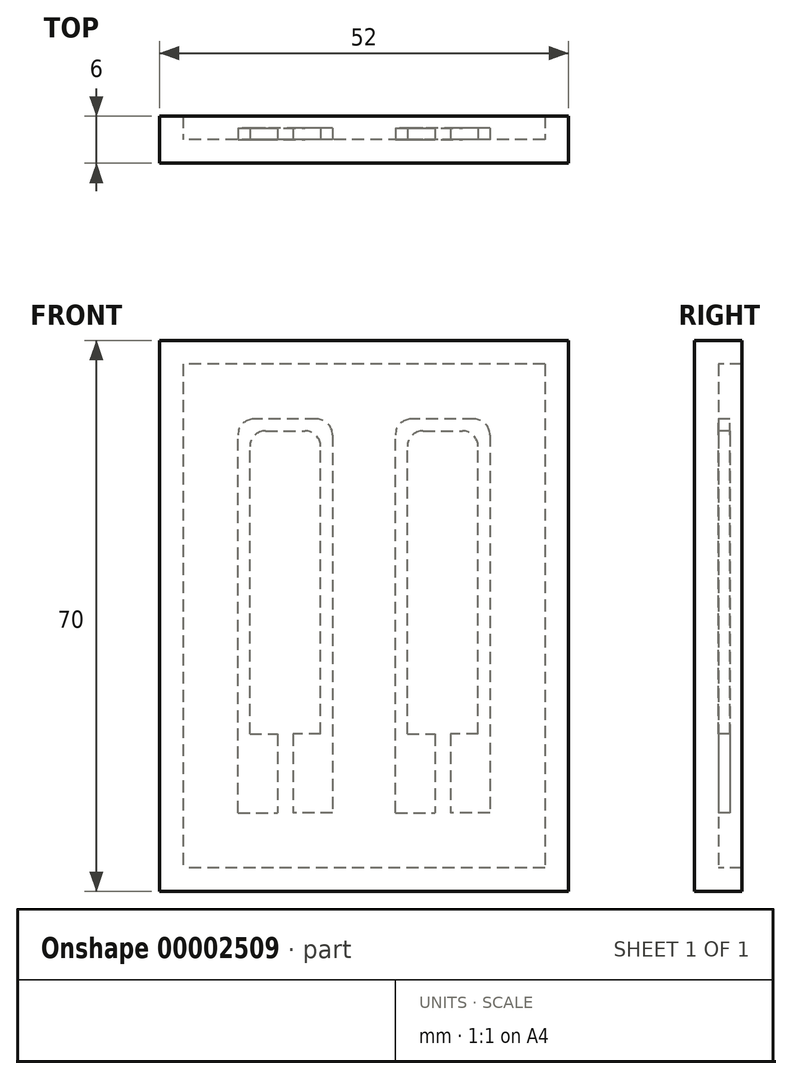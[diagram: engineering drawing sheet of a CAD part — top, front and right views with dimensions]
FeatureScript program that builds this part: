
annotation { "Feature Type Name" : "Feature", "Feature Type Description" : "" }
export const myFeature = defineFeature(function(context is Context, id is Id, definition is map)
    precondition{}
    {
        {
            var Q0;
            Q0=qCreatedBy(makeId("Front.planeOp"),FACE);
            var sketch = newSketch(context, id + "F0", { "sketchPlane" : qUnion([Q0])});
            skLineSegment(sketch, "E0.bottom", {"start": v(0, 10) * mm, "end": v(-5, 10) * mm});
            skLineSegment(sketch, "E0.top", {"start": v(0, 0) * mm, "end": v(-5, 0) * mm});
            skLineSegment(sketch, "E0.left", {"start": v(0, 10) * mm, "end": v(0, 0) * mm});
            skLineSegment(sketch, "E0.right", {"start": v(-5, 10) * mm, "end": v(-5, 0) * mm});
            skLineSegment(sketch, "E1", {"start": v(0, 10) * mm, "end": v(0, 48) * mm});
            skLineSegment(sketch, "E2", {"start": v(-1.5, 10) * mm, "end": v(-1.5, 46.5) * mm});
            skLineSegment(sketch, "E3", {"start": v(-6, -15.68) * mm, "end": v(-6, 74.56) * mm, "construction": true});
            skLineSegment(sketch, "E4", {"start": v(-3.5, 48.5) * mm, "end": v(-6, 48.5) * mm});
            skLineSegment(sketch, "E5", {"start": v(-2, 50) * mm, "end": v(-6, 50) * mm});
            skLineSegment(sketch, "E6.0.MirrorCS", {"start": v(-12, 0) * mm, "end": v(-7, 0) * mm});
            skLineSegment(sketch, "E6.1.MirrorCS", {"start": v(-12, 10) * mm, "end": v(-7, 10) * mm});
            skLineSegment(sketch, "E6.2.MirrorCS", {"start": v(-12, 10) * mm, "end": v(-12, 48) * mm});
            skLineSegment(sketch, "E6.3.MirrorCS", {"start": v(-8.5, 48.5) * mm, "end": v(-6, 48.5) * mm});
            skLineSegment(sketch, "E6.4.MirrorCS", {"start": v(-10.5, 10) * mm, "end": v(-10.5, 46.5) * mm});
            skLineSegment(sketch, "E6.5.MirrorCS", {"start": v(-7, 10) * mm, "end": v(-7, 0) * mm});
            skLineSegment(sketch, "E6.6.MirrorCS", {"start": v(-12, 10) * mm, "end": v(-12, 0) * mm});
            skLineSegment(sketch, "E6.7.MirrorCS", {"start": v(-10, 50) * mm, "end": v(-6, 50) * mm});
            skLineSegment(sketch, "E7.1.0.0", {"start": v(20, 10) * mm, "end": v(20, 48) * mm});
            skLineSegment(sketch, "E7.1.0.1", {"start": v(8, 10) * mm, "end": v(8, 48) * mm});
            skLineSegment(sketch, "E7.1.0.2", {"start": v(15, 10) * mm, "end": v(15, 0) * mm});
            skLineSegment(sketch, "E7.1.0.3", {"start": v(8, 10) * mm, "end": v(8, 0) * mm});
            skLineSegment(sketch, "E7.1.0.4", {"start": v(13, 10) * mm, "end": v(13, 0) * mm});
            skLineSegment(sketch, "E7.1.0.5", {"start": v(9.5, 10) * mm, "end": v(9.5, 46.5) * mm});
            skLineSegment(sketch, "E7.1.0.6", {"start": v(20, 10) * mm, "end": v(20, 0) * mm});
            skLineSegment(sketch, "E7.1.0.7", {"start": v(18.5, 10) * mm, "end": v(18.5, 46.5) * mm});
            skLineSegment(sketch, "E7.1.0.8", {"start": v(11.5, 48.5) * mm, "end": v(14, 48.5) * mm});
            skLineSegment(sketch, "E7.1.0.9", {"start": v(10, 50) * mm, "end": v(14, 50) * mm});
            skLineSegment(sketch, "E7.1.0.10", {"start": v(18, 50) * mm, "end": v(14, 50) * mm});
            skLineSegment(sketch, "E7.1.0.11", {"start": v(8, 0) * mm, "end": v(13, 0) * mm});
            skLineSegment(sketch, "E7.1.0.12", {"start": v(8, 10) * mm, "end": v(13, 10) * mm});
            skLineSegment(sketch, "E7.1.0.13", {"start": v(16.5, 48.5) * mm, "end": v(14, 48.5) * mm});
            skLineSegment(sketch, "E7.1.0.14", {"start": v(20, 0) * mm, "end": v(15, 0) * mm});
            skLineSegment(sketch, "E7.1.0.15", {"start": v(20, 10) * mm, "end": v(15, 10) * mm});
            skLineSegment(sketch, "E7.direction1", {"start": v(0, 10) * mm, "end": v(20, 10) * mm, "construction": true});
            skPoint(sketch, "E8.visualSharp", {"position": v(18.5, 48.5) * mm});
            skArc(sketch, "E8.filletArc", {"start": v(18.5, 46.5) * mm, "mid": v(17.91, 47.91) * mm, "end": v(16.5, 48.5) * mm});
            skPoint(sketch, "E9.visualSharp", {"position": v(20, 50) * mm});
            skArc(sketch, "E9.filletArc", {"start": v(20, 48) * mm, "mid": v(19.41, 49.41) * mm, "end": v(18, 50) * mm});
            skPoint(sketch, "E10.visualSharp", {"position": v(9.5, 48.5) * mm});
            skArc(sketch, "E10.filletArc", {"start": v(11.5, 48.5) * mm, "mid": v(10.09, 47.91) * mm, "end": v(9.5, 46.5) * mm});
            skPoint(sketch, "E11.visualSharp", {"position": v(8, 50) * mm});
            skArc(sketch, "E11.filletArc", {"start": v(10, 50) * mm, "mid": v(8.59, 49.41) * mm, "end": v(8, 48) * mm});
            skPoint(sketch, "E12.visualSharp", {"position": v(0, 50) * mm});
            skArc(sketch, "E12.filletArc", {"start": v(0, 48) * mm, "mid": v(-0.59, 49.41) * mm, "end": v(-2, 50) * mm});
            skPoint(sketch, "E13.visualSharp", {"position": v(-1.5, 48.5) * mm});
            skArc(sketch, "E13.filletArc", {"start": v(-1.5, 46.5) * mm, "mid": v(-2.09, 47.91) * mm, "end": v(-3.5, 48.5) * mm});
            skPoint(sketch, "E14.visualSharp", {"position": v(-10.5, 48.5) * mm});
            skArc(sketch, "E14.filletArc", {"start": v(-8.5, 48.5) * mm, "mid": v(-9.91, 47.91) * mm, "end": v(-10.5, 46.5) * mm});
            skPoint(sketch, "E15.visualSharp", {"position": v(-12, 50) * mm});
            skArc(sketch, "E15.filletArc", {"start": v(-10, 50) * mm, "mid": v(-11.41, 49.41) * mm, "end": v(-12, 48) * mm});
            skLineSegment(sketch, "E16.bottom", {"start": v(27, 57) * mm, "end": v(-19, 57) * mm});
            skLineSegment(sketch, "E16.top", {"start": v(27, -7) * mm, "end": v(-19, -7) * mm});
            skLineSegment(sketch, "E16.left", {"start": v(27, 57) * mm, "end": v(27, -7) * mm});
            skLineSegment(sketch, "E16.right", {"start": v(-19, 57) * mm, "end": v(-19, -7) * mm});
            skLineSegment(sketch, "E17.0", {"start": v(30, 60) * mm, "end": v(-22, 60) * mm});
            skLineSegment(sketch, "E17.1", {"start": v(30, 60) * mm, "end": v(30, -10) * mm});
            skLineSegment(sketch, "E17.2", {"start": v(30, -10) * mm, "end": v(-22, -10) * mm});
            skLineSegment(sketch, "E17.3", {"start": v(-22, 60) * mm, "end": v(-22, -10) * mm});
            skSolve(sketch);
        }
        {
            var Q0;
            {var subQ5=sQuery(id+"F0.wireOp",EDGE,"E7.1.0.0");Q0=makeQuery(id+"F0.imprint","IMPRINT",FACE,{"disambiguationData":[TD([[makeQuery(id+"F0.imprint","IMPRINT",EDGE,{"derivedFrom":subQ5}),1.0]])]});}
            var Q1;
            {var subQ3=sQuery(id+"F0.wireOp",EDGE,"E7.1.0.3");Q1=makeQuery(id+"F0.imprint","IMPRINT",FACE,{"disambiguationData":[TD([[makeQuery(id+"F0.imprint","IMPRINT",EDGE,{"derivedFrom":subQ3}),1.0]])]});}
            var Q2;
            {var subQ2=sQuery(id+"F0.wireOp",EDGE,"E7.1.0.2");Q2=makeQuery(id+"F0.imprint","IMPRINT",FACE,{"disambiguationData":[TD([[makeQuery(id+"F0.imprint","IMPRINT",EDGE,{"derivedFrom":subQ2}),1.0]])]});}
            var Q3;
            Q3=makeQuery(id+"F0.imprint","IMPRINT",FACE,{"disambiguationData":[TD([[makeQuery(id+"F0.imprint","IMPRINT",EDGE,{"derivedFrom":sQuery(id+"F0.wireOp",EDGE,"E0.top")}),1.0]])]});
            var Q4;
            Q4=makeQuery(id+"F0.imprint","IMPRINT",FACE,{"disambiguationData":[TD([[makeQuery(id+"F0.imprint","IMPRINT",EDGE,{"derivedFrom":sQuery(id+"F0.wireOp",EDGE,"E0.top")}),-1.0]])]});
            var Q5;
            {var subQ4=sQuery(id+"F0.wireOp",EDGE,"E1");Q5=makeQuery(id+"F0.imprint","IMPRINT",FACE,{"disambiguationData":[TD([[makeQuery(id+"F0.imprint","IMPRINT",EDGE,{"derivedFrom":subQ4}),1.0]])]});}
            var Q6;
            Q6=makeQuery(id+"F0.imprint","IMPRINT",FACE,{"disambiguationData":[TD([[makeQuery(id+"F0.imprint","IMPRINT",EDGE,{"derivedFrom":sQuery(id+"F0.wireOp",EDGE,"E6.0.MirrorCS")}),1.0]])]});
            var Q7;
            Q7=makeQuery(id+"F0.imprint","IMPRINT",FACE,{"disambiguationData":[TD([[makeQuery(id+"F0.imprint","IMPRINT",EDGE,{"derivedFrom":sQuery(id+"F0.wireOp",EDGE,"E16.bottom")}),-1.0]])]});
            extrude(context, id + "F1", {"entities" : qUnion([Q0, Q1, Q2, Q3, Q4, Q5, Q6, Q7]), "depth" : 3 * mm});
        }
        {
            var Q0;
            Q0=makeQuery(id+"F0.imprint","IMPRINT",FACE,{"disambiguationData":[TD([[makeQuery(id+"F0.imprint","IMPRINT",EDGE,{"derivedFrom":sQuery(id+"F0.wireOp",EDGE,"E16.bottom")}),-1.0]])]});
            extrude(context, id + "F2", {"entities" : qUnion([Q0]), "operationType" : NewBodyOperationType.ADD, "oppositeDirection" : true, "depth" : 3 * mm});
        }
        {
            var Q0;
            {var subQ2=sQuery(id+"F0.wireOp",EDGE,"E7.1.0.2");Q0=makeQuery(id+"F0.imprint","IMPRINT",FACE,{"disambiguationData":[TD([[makeQuery(id+"F0.imprint","IMPRINT",EDGE,{"derivedFrom":subQ2}),1.0]])]});}
            var Q1;
            {var subQ5=sQuery(id+"F0.wireOp",EDGE,"E7.1.0.0");Q1=makeQuery(id+"F0.imprint","IMPRINT",FACE,{"disambiguationData":[TD([[makeQuery(id+"F0.imprint","IMPRINT",EDGE,{"derivedFrom":subQ5}),1.0]])]});}
            var Q2;
            {var subQ3=sQuery(id+"F0.wireOp",EDGE,"E7.1.0.3");Q2=makeQuery(id+"F0.imprint","IMPRINT",FACE,{"disambiguationData":[TD([[makeQuery(id+"F0.imprint","IMPRINT",EDGE,{"derivedFrom":subQ3}),1.0]])]});}
            var Q3;
            Q3=makeQuery(id+"F0.imprint","IMPRINT",FACE,{"disambiguationData":[TD([[makeQuery(id+"F0.imprint","IMPRINT",EDGE,{"derivedFrom":sQuery(id+"F0.wireOp",EDGE,"E0.top")}),-1.0]])]});
            var Q4;
            {var subQ4=sQuery(id+"F0.wireOp",EDGE,"E1");Q4=makeQuery(id+"F0.imprint","IMPRINT",FACE,{"disambiguationData":[TD([[makeQuery(id+"F0.imprint","IMPRINT",EDGE,{"derivedFrom":subQ4}),1.0]])]});}
            var Q5;
            Q5=makeQuery(id+"F0.imprint","IMPRINT",FACE,{"disambiguationData":[TD([[makeQuery(id+"F0.imprint","IMPRINT",EDGE,{"derivedFrom":sQuery(id+"F0.wireOp",EDGE,"E6.0.MirrorCS")}),1.0]])]});
            extrude(context, id + "F3", {"entities" : qUnion([Q0, Q1, Q2, Q3, Q4, Q5]), "operationType" : NewBodyOperationType.ADD, "oppositeDirection" : true, "depth" : 1.5 * mm});
        }
    });
